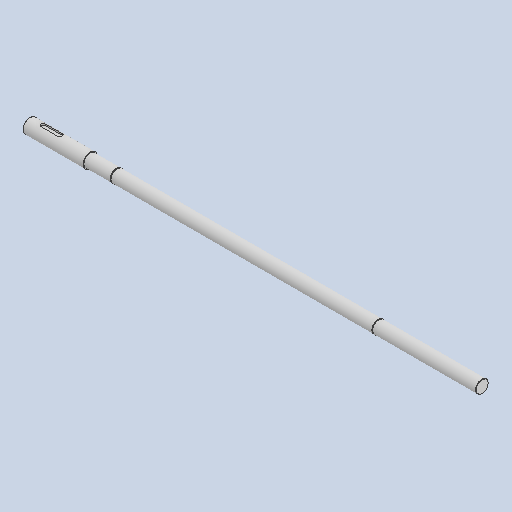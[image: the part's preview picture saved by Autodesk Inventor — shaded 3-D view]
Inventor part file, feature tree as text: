
AUTODESK INVENTOR PART (.ipt)
format: ipt  version: 2025 (Build 290162010, 162A)  size: 311,296 bytes
history: native  units: mm
features: other x10, chamfer x2, revolve x1
ambient origin geometry x6: Origin, XZ Plane, XY Plane, X Axis, Y Axis, Z Axis
bodies: Solid1 (feature_tree)
feature tree (13):
  other  "{BB8FE430-83BF-418D-8DF9-9B323D3DB9B9}"
  revolve  "Revolution1"  [1 undecoded]
  chamfer  "Chamfer1"  Distance=19.0mm
  other  "Keyway1"
  chamfer  "Chamfer2"  Distance=17.0mm
  other  "Retaining Ring Groove1"
  other  "Retaining Ring Groove2"
  other  "Start Plane"
  other  "Origin point"
  other  "Main Sketch"
  other  "iFeature11:1"
  other  "iFeature27:1"
  other  "iFeature27:2"
note: 1 required parameter value undecoded (feature->parameter linkage not recoverable at this tier; creation-order binding heuristic only, values carry confidence <= 0.55)
